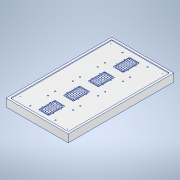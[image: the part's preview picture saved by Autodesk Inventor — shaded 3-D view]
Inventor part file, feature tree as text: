
AUTODESK INVENTOR PART (.ipt)
format: ipt  version: 2022 (Build 260153000, 153)  size: 509,440 bytes
history: native  units: in
note: dims shown in document units (in); Inventor stores cm internally (conversion verified against a paired STEP export)
features: sketch x6, extrude x3, hole x3, other x2
ambient origin geometry x8: Origin, YZ Plane, XZ Plane, XY Plane, X Axis, Y Axis, Z Axis, Center Point
bodies: Solid1 (feature_tree)
feature tree (14):
  other  "Annotations"
  extrude  "Extrusion1"  Depth=8.5in
  extrude  "Extrusion2"  Depth=0.1713in
  hole  "Hole1"  [1 undecoded]
  hole  "Hole2"  [1 undecoded]
  hole  "Hole3"  [1 undecoded]
  extrude  "Extrusion3"  Depth=2.0in
  sketch  "Sketch1"  dims[d0=5.0in d1=8.5in]
  sketch  "Sketch2"  dims[d2=0.625in d3=0.0in d4=0.1713in]
  sketch  "Sketch3"  dims[d5=0.1713in d6=0.1713in]
  sketch  "Sketch4"  dims[d7=0.063in d8=0.0in d9=1.2756in]
  sketch  "Sketch5"  dims[d10=0.3287in d11=1.4213in]
  sketch  "Sketch6"  dims[d12=2.0276in d13=1.5748in d15=2.0in d16=0.3937in d18=0.3937in d20=0.0984in d21=0.2362in d22=0.1575in d23=0.0787in d24=90.0deg d25=0.315in d26=0.8108in d35=1.8262in d36=0.7244in d37=0.6299in d38=0.9264in d39=1.5748in d41=2.0in d42=0.3937in d44=0.3937in d46=0.0402in d47=0.094in d48=0.1575in d49=0.0787in d50=90.0deg d51=0.315in d52=0.8108in d53=0.5394in d54=2.0394in d55=3.5433in d57=0.125in d58=1.9685in d60=0.125in d63=1.5748in d65=2.0in d66=0.3937in d68=0.3937in d70=0.063in d71=0.094in d72=0.1575in d73=0.0787in d74=90.0deg d75=0.315in d76=0.8108in d77=0.0787in d79=0.0827in d80=0.0827in d81=0.0827in d82=0.0827in d83=0.08in d84=0.08in d85=0.08in d86=0.08in d87=0.0591in d88=0.0591in d89=1.5748in d91=2.0in d92=0.3937in d94=0.3937in d96=0.045in d97=0.0in d98=0.1457in d99=1.6293in d100=0.528in d101=2.5559in d102=7.1575in d103=1.6287in d104=7.1575in d105=2.5559in d56=0.0295in]
  other  "General Note 1"
note: 3 required parameter values undecoded (feature->parameter linkage not recoverable at this tier; creation-order binding heuristic only, values carry confidence <= 0.55)
